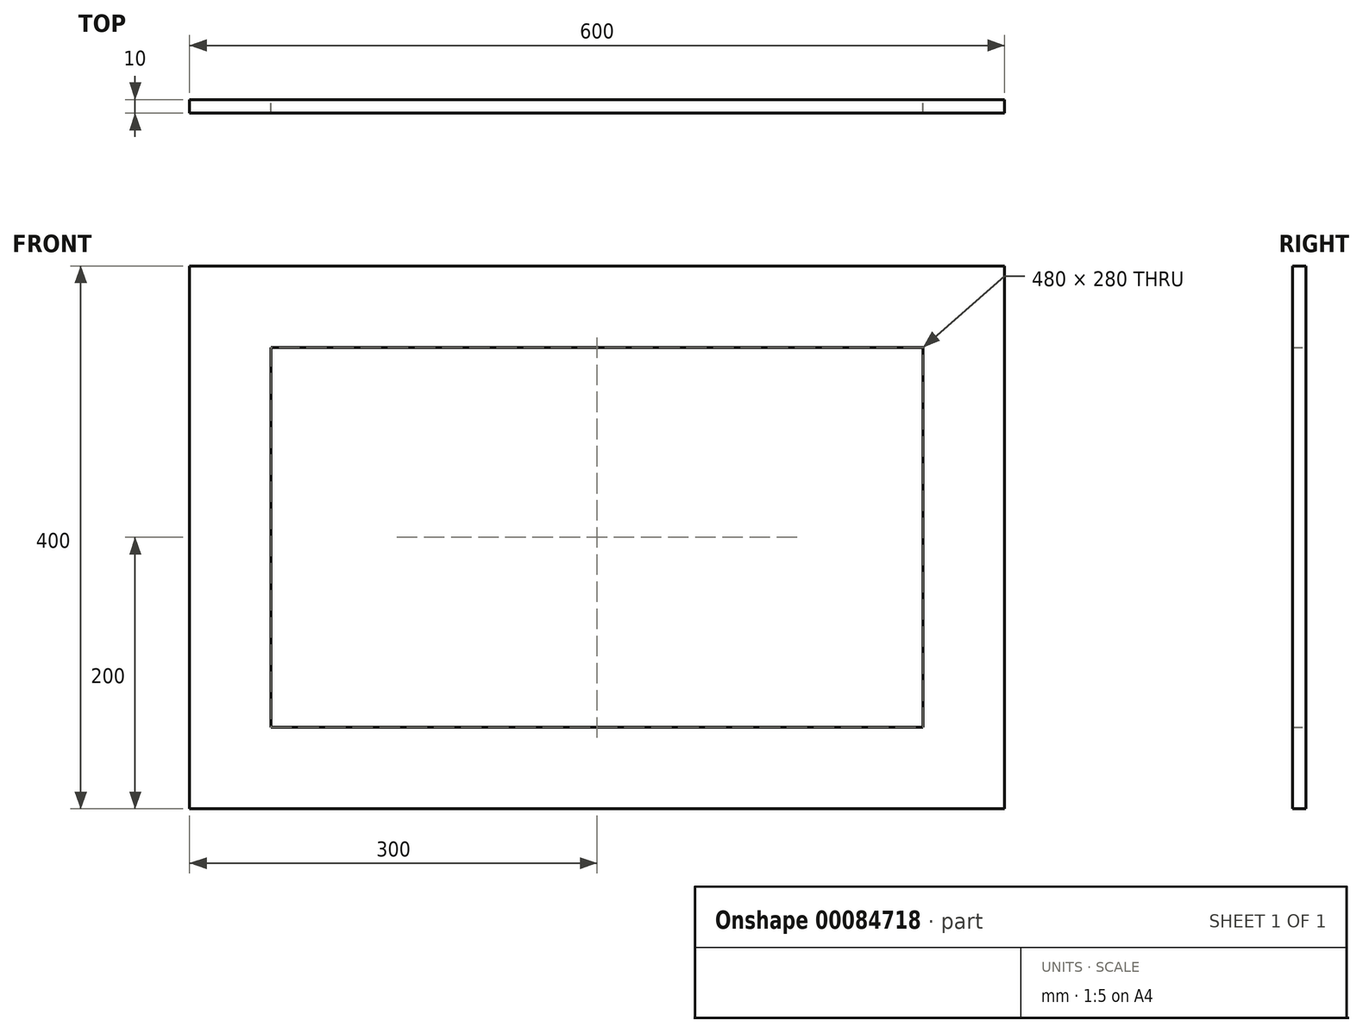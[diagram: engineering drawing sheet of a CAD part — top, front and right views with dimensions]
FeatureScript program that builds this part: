
annotation { "Feature Type Name" : "Feature", "Feature Type Description" : "" }
export const myFeature = defineFeature(function(context is Context, id is Id, definition is map)
    precondition{}
    {
        {
            var Q0;
            Q0=qCreatedBy(makeId("Front.planeOp"),FACE);
            var sketch = newSketch(context, id + "F0", { "sketchPlane" : qUnion([Q0])});
            skLineSegment(sketch, "E0.bottom", {"start": v(300, 200) * mm, "end": v(-300, 200) * mm});
            skLineSegment(sketch, "E0.top", {"start": v(300, -200) * mm, "end": v(-300, -200) * mm});
            skLineSegment(sketch, "E0.left", {"start": v(300, 200) * mm, "end": v(300, -200) * mm});
            skLineSegment(sketch, "E0.right", {"start": v(-300, 200) * mm, "end": v(-300, -200) * mm});
            skPoint(sketch, "E0.middle", {"position": v(0, 0) * mm});
            skLineSegment(sketch, "E1.bottom", {"start": v(240, 140) * mm, "end": v(-240, 140) * mm});
            skLineSegment(sketch, "E1.top", {"start": v(240, -140) * mm, "end": v(-240, -140) * mm});
            skLineSegment(sketch, "E1.left", {"start": v(240, 140) * mm, "end": v(240, -140) * mm});
            skLineSegment(sketch, "E1.right", {"start": v(-240, 140) * mm, "end": v(-240, -140) * mm});
            skSolve(sketch);
        }
        {
            var Q0;
            Q0=makeQuery(id+"F0.imprint","IMPRINT",FACE,{"disambiguationData":[TD([[makeQuery(id+"F0.imprint","IMPRINT",EDGE,{"derivedFrom":sQuery(id+"F0.wireOp",EDGE,"E0.bottom")}),1.0]])]});
            extrude(context, id + "F1", {"entities" : qUnion([Q0]), "depth" : 10 * mm});
        }
    });
